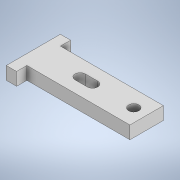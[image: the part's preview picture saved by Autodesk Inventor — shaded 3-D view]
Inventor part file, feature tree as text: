
AUTODESK INVENTOR PART (.ipt)
format: ipt  version: 2022 (Build 260153000, 153)  size: 116,736 bytes
history: native  units: mm
features: extrude x2, sketch x2
ambient origin geometry x8: Origin, YZ Plane, XZ Plane, XY Plane, X Axis, Y Axis, Z Axis, Center Point
bodies: Solid1 (feature_tree)
feature tree (4):
  extrude  "Extrusion1"  Depth=4.0mm
  extrude  "Extrusion2"  Depth=4.0mm
  sketch  "Sketch1"  dims[d0=40.0mm d5=4.0mm]
  sketch  "Sketch2"  dims[d6=5.0mm d7=0.0mm d8=4.0mm d10=4.0mm d11=12.0mm d12=4.0mm d13=7.75mm d14=0.0mm]
